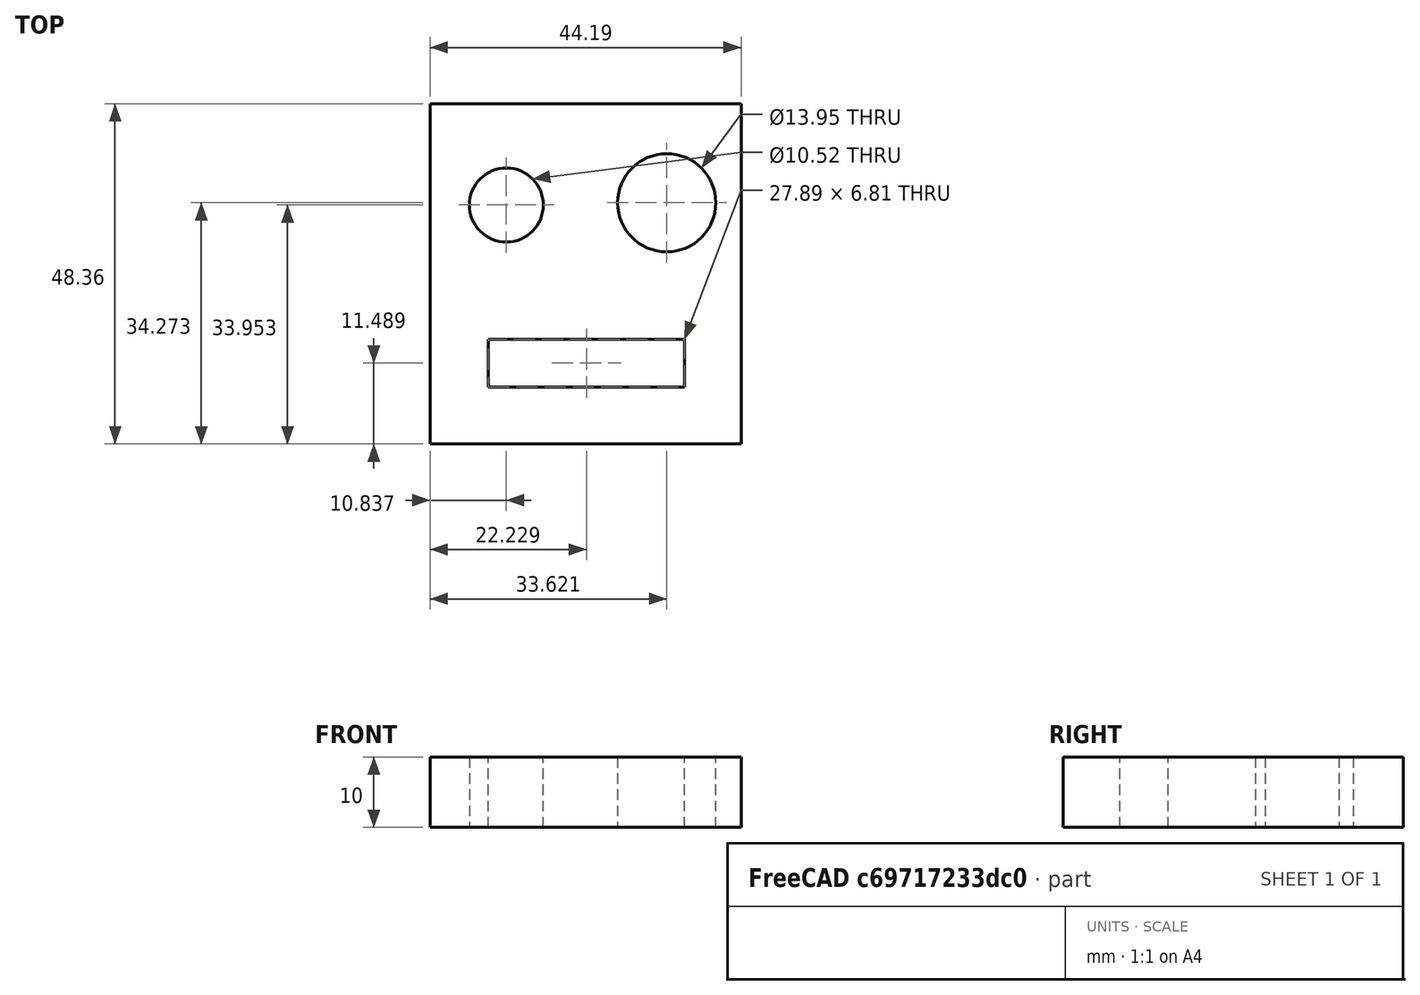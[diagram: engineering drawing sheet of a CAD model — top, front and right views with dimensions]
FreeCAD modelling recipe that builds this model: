
FCSTD DOCUMENT  (FreeCAD 1.0R38806 (Git))
Label: reto_2
License: All rights reserved
LicenseURL: https://en.wikipedia.org/wiki/All_rights_reserved
objects: Sketcher::SketchObject×1, Part::Extrusion×1
note: 3 computed .brp shape members not serialized (recipe doc carries the construction recipe); baked Part::Feature solids carry a one-line shape summary decoded from their .brp

FEATURE [Sketcher::SketchObject] Sketch
  ArcFitTolerance = 1e-06
  FullyConstrained = false
  MakeInternals = false
  sketch-geometry (10):
    g0: LineSegment StartX=0 StartY=0 StartZ=0 EndX=44.1939 EndY=0 EndZ=0
    g1: LineSegment StartX=44.1939 StartY=0 StartZ=0 EndX=44.1939 EndY=48.3607 EndZ=0
    g2: LineSegment StartX=44.1939 StartY=48.3607 StartZ=0 EndX=0 EndY=48.3607 EndZ=0
    g3: LineSegment StartX=0 StartY=48.3607 StartZ=0 EndX=0 EndY=0 EndZ=0
    g4: Circle CenterX=33.6212 CenterY=34.2726 CenterZ=0 NormalX=0 NormalY=0 NormalZ=1 AngleXU=0 Radius=6.97501
    g5: Circle CenterX=10.8373 CenterY=33.9532 CenterZ=0 NormalX=0 NormalY=0 NormalZ=1 AngleXU=0 Radius=5.26016
    g6: LineSegment StartX=8.28209 StartY=8.0817 StartZ=0 EndX=36.1764 EndY=8.0817 EndZ=0
    g7: LineSegment StartX=36.1764 StartY=8.0817 StartZ=0 EndX=36.1764 EndY=14.8956 EndZ=0
    g8: LineSegment StartX=36.1764 StartY=14.8956 StartZ=0 EndX=8.28209 EndY=14.8956 EndZ=0
    g9: LineSegment StartX=8.28209 StartY=14.8956 StartZ=0 EndX=8.28209 EndY=8.0817 EndZ=0
  constraints (16):
    c: Coincident(g0,g1)
    c: Coincident(g1,g2)
    c: Coincident(g2,g3)
    c: Coincident(g3,g0)
    c: Horizontal(g0)
    c: Horizontal(g2)
    c: Vertical(g1)
    c: Vertical(g3)
    c: Coincident(g6,g7)
    c: Coincident(g7,g8)
    c: Coincident(g8,g9)
    c: Coincident(g9,g6)
    c: Horizontal(g6)
    c: Horizontal(g8)
    c: Vertical(g7)
    c: Vertical(g9)
FEATURE [Part::Extrusion] Extrude
  Base = -> Sketch
  Dir = (0,0,1)
  DirMode = 2
  FaceMakerClass = Part::FaceMakerBullseye
  FaceMakerMode = 3
  LengthFwd = 10
  LengthRev = 0
  Solid = true
  Symmetric = false
